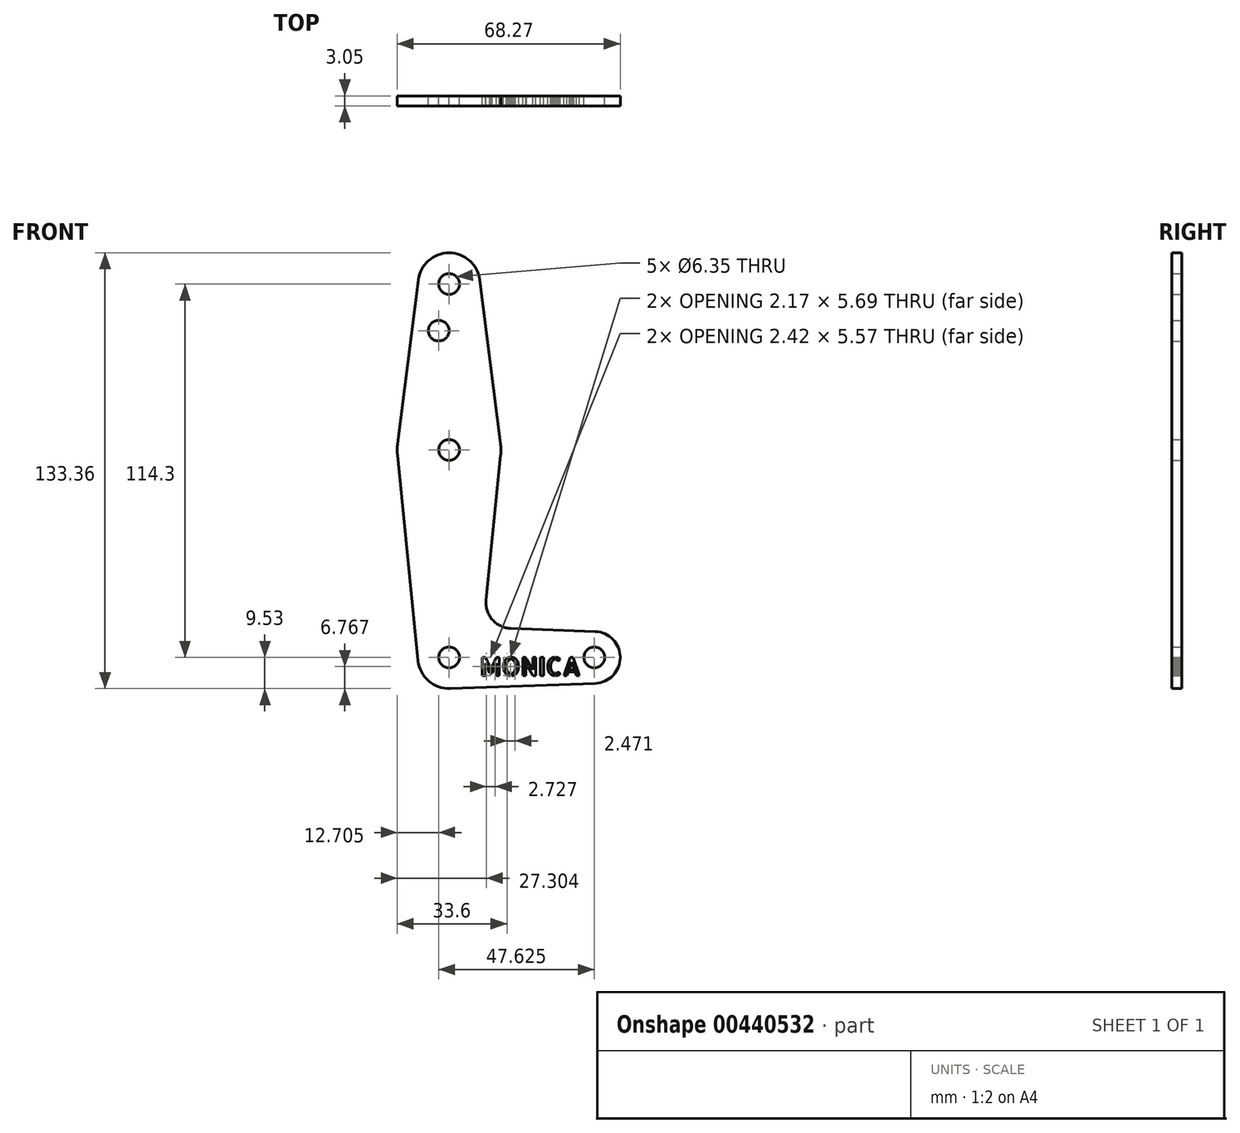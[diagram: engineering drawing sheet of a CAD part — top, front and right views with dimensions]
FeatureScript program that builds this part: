
annotation { "Feature Type Name" : "Feature", "Feature Type Description" : "" }
export const myFeature = defineFeature(function(context is Context, id is Id, definition is map)
    precondition{}
    {
        {
            var Q0;
            Q0=qCreatedBy(makeId("Front.planeOp"),FACE);
            var sketch = newSketch(context, id + "F0", { "sketchPlane" : qUnion([Q0])});
            skLineSegment(sketch, "E0", {"start": v(0, 114.3) * mm, "end": v(0, 0) * mm, "construction": true});
            skLineSegment(sketch, "E1", {"start": v(0, 0) * mm, "end": v(44.45, 0) * mm, "construction": true});
            skCircle(sketch, "E2", {"center": v(0, 114.3) * mm, "radius": 9.53 * mm});
            skCircle(sketch, "E3", {"center": v(0, 0) * mm, "radius": 9.53 * mm});
            skCircle(sketch, "E4", {"center": v(0, 63.5) * mm, "radius": 15.88 * mm});
            skCircle(sketch, "E5", {"center": v(44.45, 0) * mm, "radius": 7.94 * mm});
            skLineSegment(sketch, "E6", {"start": v(-9.45, 115.5) * mm, "end": v(-15.75, 65.48) * mm});
            skLineSegment(sketch, "E7", {"start": v(9.45, 115.5) * mm, "end": v(15.75, 65.48) * mm});
            skLineSegment(sketch, "E8", {"start": v(18.97, 8.85) * mm, "end": v(44.73, 7.93) * mm});
            skLineSegment(sketch, "E9", {"start": v(0.34, -9.52) * mm, "end": v(44.73, -7.93) * mm});
            skLineSegment(sketch, "E10", {"start": v(-15.8, 61.91) * mm, "end": v(-9.48, -0.95) * mm});
            skLineSegment(sketch, "E11", {"start": v(15.8, 61.91) * mm, "end": v(11.34, 17.6) * mm});
            skCircle(sketch, "E12", {"center": v(0, 114.3) * mm, "radius": 3.18 * mm});
            skCircle(sketch, "E13", {"center": v(-3.17, 100.03) * mm, "radius": 3.18 * mm});
            skCircle(sketch, "E14", {"center": v(0, 63.5) * mm, "radius": 3.18 * mm});
            skCircle(sketch, "E15", {"center": v(0, 0) * mm, "radius": 3.18 * mm});
            skCircle(sketch, "E16", {"center": v(44.45, 0) * mm, "radius": 3.18 * mm});
            skArc(sketch, "E17.filletArc", {"start": v(11.34, 17.6) * mm, "mid": v(13.26, 11.57) * mm, "end": v(18.97, 8.85) * mm});
            skText(sketch, "E18", { "text": "MONICA", "fontName": "AllertaStencil-Regular.ttf"});
            const initialGuessF0  = {"E18": [0.00952, -0.00557, 1, 0, 0.00557]};
            skSetInitialGuess(sketch, initialGuessF0);
            skSolve(sketch);
        }
        {
            var Q0;
            Q0 = qSketchRegion(id + "F0", true);
            extrude(context, id + "F1", {"entities" : qUnion([Q0]), "depth" : 3.05 * mm});
        }
    });
